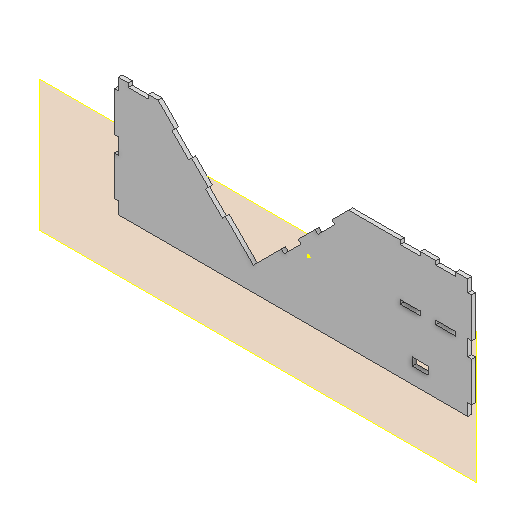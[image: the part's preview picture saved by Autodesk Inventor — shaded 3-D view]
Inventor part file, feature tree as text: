
AUTODESK INVENTOR PART (.ipt)
format: ipt  version: 2022 (Build 260153000, 153)  size: 265,728 bytes
history: native  units: mm
features: sketch x5, reference x5, other x5, extrude x3, projected_geometry x2, plane x1
ambient origin geometry x8: Origin, YZ Plane, XZ Plane, XY Plane, X Axis, Y Axis, Z Axis, Center Point
bodies: Solid1 (feature_tree)
feature tree (21):
  plane  "Work Plane1"
  extrude  "Extrusion1"  Depth=25.0mm
  sketch  "Sketch3"  dims[d17=5.0mm d18=80.0mm]
  extrude  "Extrusion3"  Depth=80.0mm
  sketch  "Sketch5"  dims[d22=15.0mm]
  extrude  "Extrusion4"  Depth=5.0mm
  sketch  "Sketch1"  dims[d0=5.0mm d1=0.0mm d16=25.0mm]
  reference  "Reference1"
  reference  "Reference2"
  reference  "Reference3"
  reference  "Reference4"
  reference  "Reference5"
  sketch  "Sketch4"  dims[d19=25.0mm d20=5.0mm]
  projected_geometry  "Projected Loop2"
  sketch  "Sketch6"  dims[d23=5.0mm d24=0.0mm d25=20.0mm d26=20.0mm d27=10.0mm d28=20.0mm d29=50.0mm d30=10.0mm d31=0.0mm]
  projected_geometry  "Projected Loop3"
  parser-record x1  (decoder bookkeeping rows leaked as tree rows — omitted from the tree; the rows remain in map.json)
  other  "Ensamble caja.iam"
  other  "Modelo base:1"
  other  "Lateral:1"
  other  "Lateral:2"
note: 1 file-system path scrubbed to <path> (originals preserved in map.json)
